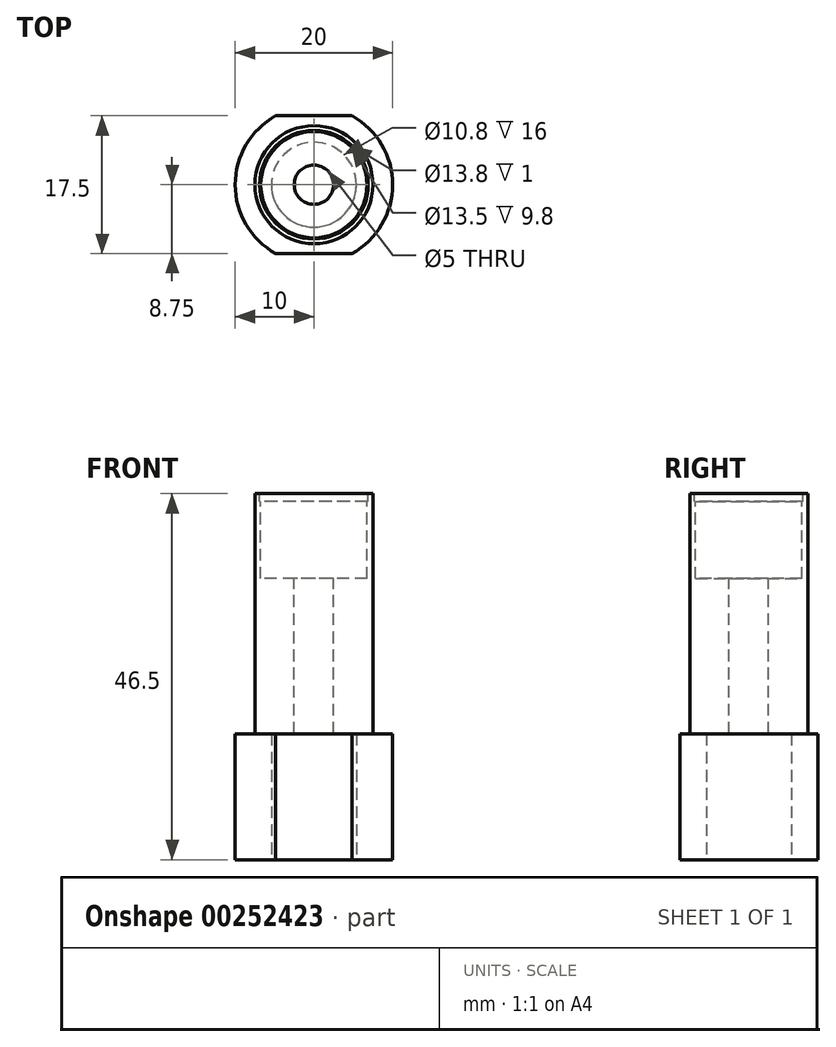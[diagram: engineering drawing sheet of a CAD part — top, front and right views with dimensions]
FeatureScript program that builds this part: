
annotation { "Feature Type Name" : "Feature", "Feature Type Description" : "" }
export const myFeature = defineFeature(function(context is Context, id is Id, definition is map)
    precondition{}
    {
        {
            var Q0;
            Q0=qCreatedBy(makeId("Top.planeOp"),FACE);
            var sketch = newSketch(context, id + "F0", { "sketchPlane" : qUnion([Q0])});
            skLineSegment(sketch, "E0.bottom", {"start": v(6.5, -6.5) * mm, "end": v(-6.5, -6.5) * mm});
            skLineSegment(sketch, "E0.top", {"start": v(6.5, 6.5) * mm, "end": v(-6.5, 6.5) * mm});
            skLineSegment(sketch, "E0.left", {"start": v(6.5, -6.5) * mm, "end": v(6.5, 6.5) * mm});
            skLineSegment(sketch, "E0.right", {"start": v(-6.5, -6.5) * mm, "end": v(-6.5, 6.5) * mm});
            skPoint(sketch, "E0.middle", {"position": v(0, 0) * mm});
            skSolve(sketch);
        }
        {
            var Q0;
            Q0 = qSketchRegion(id + "F0", true);
            extrude(context, id + "F1", {"entities" : qUnion([Q0]), "depth" : 16 * mm});
        }
        {
            var Q0;
            Q0=makeQuery(id+"F1.opExtrude","CAP_FACE",FACE,{"disambiguationData":[OSD([sQuery(id+"F0.wireOp",EDGE,"E0.bottom"),sQuery(id+"F0.wireOp",EDGE,"E0.top"),sQuery(id+"F0.wireOp",EDGE,"E0.left"),sQuery(id+"F0.wireOp",EDGE,"E0.right")])],"isStart":true});
            var sketch = newSketch(context, id + "F2", { "sketchPlane" : qUnion([Q0])});
            skPoint(sketch, "E1", {"position": v(0, 0) * mm});
            skSolve(sketch);
        }
        {
            var Q0;
            Q0=sQuery(id+"F2.wireOp",VERTEX,"E1");
            var Q1;
            Q1=makeQuery(id+"F1.opExtrude","SWEPT_BODY",BODY,{"disambiguationData":[OSD([sQuery(id+"F0.wireOp",EDGE,"E0.bottom"),sQuery(id+"F0.wireOp",EDGE,"E0.top"),sQuery(id+"F0.wireOp",EDGE,"E0.left"),sQuery(id+"F0.wireOp",EDGE,"E0.right")])]});
            hole(context, id + "F3", {"style" : HoleStyle.SIMPLE, "endStyle" : HoleEndStyle.THROUGH, "standardTappedOrClearance" : lookupTablePath({ "standard" : "ISO", "engagement" : "75%", "pitch" : "1.25 mm", "size" : "M12", "type" : "Tapped" }), "standardBlindInLast" : lookupTablePath({ "standard" : "ISO", "engagement" : "75%", "pitch" : "1.25 mm", "size" : "M12", "type" : "Tapped" }), "holeDiameter" : 10.8 * mm, "showTappedDepth" : true, "tappedDepth" : 12 * mm, "tapClearance" : 3, "startFromSketch" : true, "locations" : qUnion([Q0]), "scope" : qUnion([Q1]), "majorDiameter" : 12 * mm});
        }
        {
            var Q0;
            Q0=makeQuery(id+"F1.opExtrude","CAP_FACE",FACE,{"disambiguationData":[OSD([sQuery(id+"F0.wireOp",EDGE,"E0.bottom"),sQuery(id+"F0.wireOp",EDGE,"E0.top"),sQuery(id+"F0.wireOp",EDGE,"E0.left"),sQuery(id+"F0.wireOp",EDGE,"E0.right")])],"isStart":false});
            var sketch = newSketch(context, id + "F4", { "sketchPlane" : qUnion([Q0])});
            skCircle(sketch, "E2", {"center": v(0, 0) * mm, "radius": 7.5 * mm});
            skSolve(sketch);
        }
        {
            var Q0;
            Q0 = qSketchRegion(id + "F4", true);
            extrude(context, id + "F5", {"entities" : qUnion([Q0]), "operationType" : NewBodyOperationType.ADD, "depth" : 30.5 * mm});
        }
        {
            var Q0;
            Q0=makeQuery(id+"F5.opExtrude","CAP_FACE",FACE,{"disambiguationData":[OSD([sQuery(id+"F4.wireOp",EDGE,"E2")])],"isStart":false});
            var sketch = newSketch(context, id + "F6", { "sketchPlane" : qUnion([Q0])});
            skCircle(sketch, "E3", {"center": v(0, 0) * mm, "radius": 6.9 * mm});
            skSolve(sketch);
        }
        {
            var Q0;
            Q0 = qSketchRegion(id + "F6", true);
            extrude(context, id + "F7", {"entities" : qUnion([Q0]), "operationType" : NewBodyOperationType.REMOVE, "oppositeDirection" : true, "depth" : 1 * mm});
        }
        {
            var Q0;
            Q0=makeQuery(id+"F7.boolean.opBoolean","COPY",FACE,{"derivedFrom":makeQuery(id+"F7.opExtrude","CAP_FACE",FACE,{"disambiguationData":[OSD([sQuery(id+"F6.wireOp",EDGE,"E3")])],"isStart":false})});
            var sketch = newSketch(context, id + "F8", { "sketchPlane" : qUnion([Q0])});
            skCircle(sketch, "E4", {"center": v(0, 0) * mm, "radius": 6.75 * mm});
            skSolve(sketch);
        }
        {
            var Q0;
            Q0 = qSketchRegion(id + "F8", true);
            extrude(context, id + "F9", {"entities" : qUnion([Q0]), "operationType" : NewBodyOperationType.REMOVE, "oppositeDirection" : true, "depth" : 9.8 * mm});
        }
        {
            var Q0;
            Q0=makeQuery(id+"F9.boolean.opBoolean","COPY",FACE,{"derivedFrom":makeQuery(id+"F9.opExtrude","CAP_FACE",FACE,{"disambiguationData":[OSD([sQuery(id+"F8.wireOp",EDGE,"E4")])],"isStart":false})});
            var sketch = newSketch(context, id + "F10", { "sketchPlane" : qUnion([Q0])});
            skCircle(sketch, "E5", {"center": v(0, 0) * mm, "radius": 2.5 * mm});
            skSolve(sketch);
        }
        {
            var Q0;
            Q0=makeQuery(id+"F10.imprint","IMPRINT",FACE,{"disambiguationData":[TD([[makeQuery(id+"F10.imprint","IMPRINT",EDGE,{"derivedFrom":sQuery(id+"F10.wireOp",EDGE,"E5")}),1.0]])]});
            extrude(context, id + "F11", {"entities" : qUnion([Q0]), "operationType" : NewBodyOperationType.REMOVE, "oppositeDirection" : true, "depth" : 50 * mm});
        }
        {
            var Q0;
            Q0=makeQuery(id+"F1.opExtrude","CAP_FACE",FACE,{"disambiguationData":[OSD([sQuery(id+"F0.wireOp",EDGE,"E0.bottom"),sQuery(id+"F0.wireOp",EDGE,"E0.top"),sQuery(id+"F0.wireOp",EDGE,"E0.left"),sQuery(id+"F0.wireOp",EDGE,"E0.right")])],"isStart":true});
            var sketch = newSketch(context, id + "F12", { "sketchPlane" : qUnion([Q0])});
            skCircle(sketch, "E6", {"center": v(0, 0) * mm, "radius": 10 * mm});
            skCircle(sketch, "E7.0", {"center": v(0, 0) * mm, "radius": 5.4 * mm});
            skSolve(sketch);
        }
        {
            var Q0;
            Q0=makeQuery(id+"F12.imprint","IMPRINT",FACE,{"disambiguationData":[TD([[makeQuery(id+"F12.imprint","IMPRINT",EDGE,{"derivedFrom":sQuery(id+"F12.wireOp",EDGE,"E6")}),1.0]])]});
            var Q1;
            {var subQ0=sQuery(id+"F0.wireOp",EDGE,"E0.right");var subQ1=sQuery(id+"F0.wireOp",EDGE,"E0.top");var subQ2=makeQuery(id+"F1.opExtrude","CAP_FACE",FACE,{"disambiguationData":[OSD([sQuery(id+"F0.wireOp",EDGE,"E0.bottom"),subQ1,sQuery(id+"F0.wireOp",EDGE,"E0.left"),subQ0])],"isStart":false});Q1=makeQuery(id+"F5.boolean.opBoolean","SPLIT",FACE,{"disambiguationData":[TD([subQ2,makeQuery(id+"F1.opExtrude","SWEPT_FACE",FACE,{"disambiguationData":[OSD([subQ1])]}),makeQuery(id+"F1.opExtrude","SWEPT_FACE",FACE,{"disambiguationData":[OSD([subQ0])]}),makeQuery(id+"F5.opExtrude","SWEPT_FACE",FACE,{"disambiguationData":[OSD([sQuery(id+"F4.wireOp",EDGE,"E2")])]})])],"derivedFrom":subQ2});}
            extrude(context, id + "F13", {"entities" : qUnion([Q0]), "operationType" : NewBodyOperationType.ADD, "endBound" : BoundingType.UP_TO_SURFACE, "oppositeDirection" : true, "endBoundEntityFace" : qUnion([Q1]), "depth" : 25 * mm});
        }
        {
            var Q0;
            {var subQ0=sQuery(id+"F0.wireOp",EDGE,"E0.right");var subQ1=sQuery(id+"F0.wireOp",EDGE,"E0.left");var subQ2=sQuery(id+"F0.wireOp",EDGE,"E0.top");var subQ3=sQuery(id+"F0.wireOp",EDGE,"E0.bottom");Q0=makeQuery(id+"F13.boolean.opBoolean","MERGE",FACE,{"derivedFrom":[makeQuery(id+"F1.opExtrude","CAP_FACE",FACE,{"disambiguationData":[OSD([subQ3,subQ2,subQ1,subQ0])],"isStart":true}),makeQuery(id+"F13.opExtrude","CAP_FACE",FACE,{"disambiguationData":[OSD([subQ3,subQ2,subQ1,subQ0,sQuery(id+"F12.wireOp",EDGE,"E6")])],"isStart":true})]});}
            var sketch = newSketch(context, id + "F14", { "sketchPlane" : qUnion([Q0])});
            skLineSegment(sketch, "E8.bottom", {"start": v(-17.5, -8.75) * mm, "end": v(17.5, -8.75) * mm});
            skLineSegment(sketch, "E8.top", {"start": v(-17.5, 8.75) * mm, "end": v(17.5, 8.75) * mm});
            skLineSegment(sketch, "E8.left", {"start": v(-17.5, -8.75) * mm, "end": v(-17.5, 8.75) * mm});
            skLineSegment(sketch, "E8.right", {"start": v(17.5, -8.75) * mm, "end": v(17.5, 8.75) * mm});
            skPoint(sketch, "E8.middle", {"position": v(0, 0) * mm});
            skSolve(sketch);
        }
        {
            var Q0;
            {var subQ0=sQuery(id+"F14.wireOp",EDGE,"E8.top");var subQ1=makeQuery(id+"F13.opExtrude","CAP_EDGE",EDGE,{"disambiguationData":[OSD([sQuery(id+"F12.wireOp",EDGE,"E6")])],"isStart":true});var subQ2=makeQuery(id+"F14.imprint","INTERSECT",VERTEX,{"disambiguationData":[OD(0.0)],"derivedFrom":[subQ1,subQ0]});Q0=makeQuery(id+"F14.imprint","IMPRINT",FACE,{"disambiguationData":[TD([[makeQuery(id+"F14.imprint","IMPRINT",EDGE,{"disambiguationData":[TD([[subQ2,-1.0]])],"derivedFrom":subQ0}),1.0]])]});}
            var Q1;
            {var subQ0=sQuery(id+"F14.wireOp",EDGE,"E8.bottom");var subQ1=makeQuery(id+"F13.opExtrude","CAP_EDGE",EDGE,{"disambiguationData":[OSD([sQuery(id+"F12.wireOp",EDGE,"E6")])],"isStart":true});var subQ2=makeQuery(id+"F14.imprint","INTERSECT",VERTEX,{"disambiguationData":[OD(0.0)],"derivedFrom":[subQ1,subQ0]});Q1=makeQuery(id+"F14.imprint","IMPRINT",FACE,{"disambiguationData":[TD([[makeQuery(id+"F14.imprint","IMPRINT",EDGE,{"disambiguationData":[TD([[subQ2,-1.0]])],"derivedFrom":subQ0}),-1.0]])]});}
            extrude(context, id + "F15", {"entities" : qUnion([Q0, Q1]), "operationType" : NewBodyOperationType.REMOVE, "oppositeDirection" : true, "depth" : 25 * mm});
        }
    });
